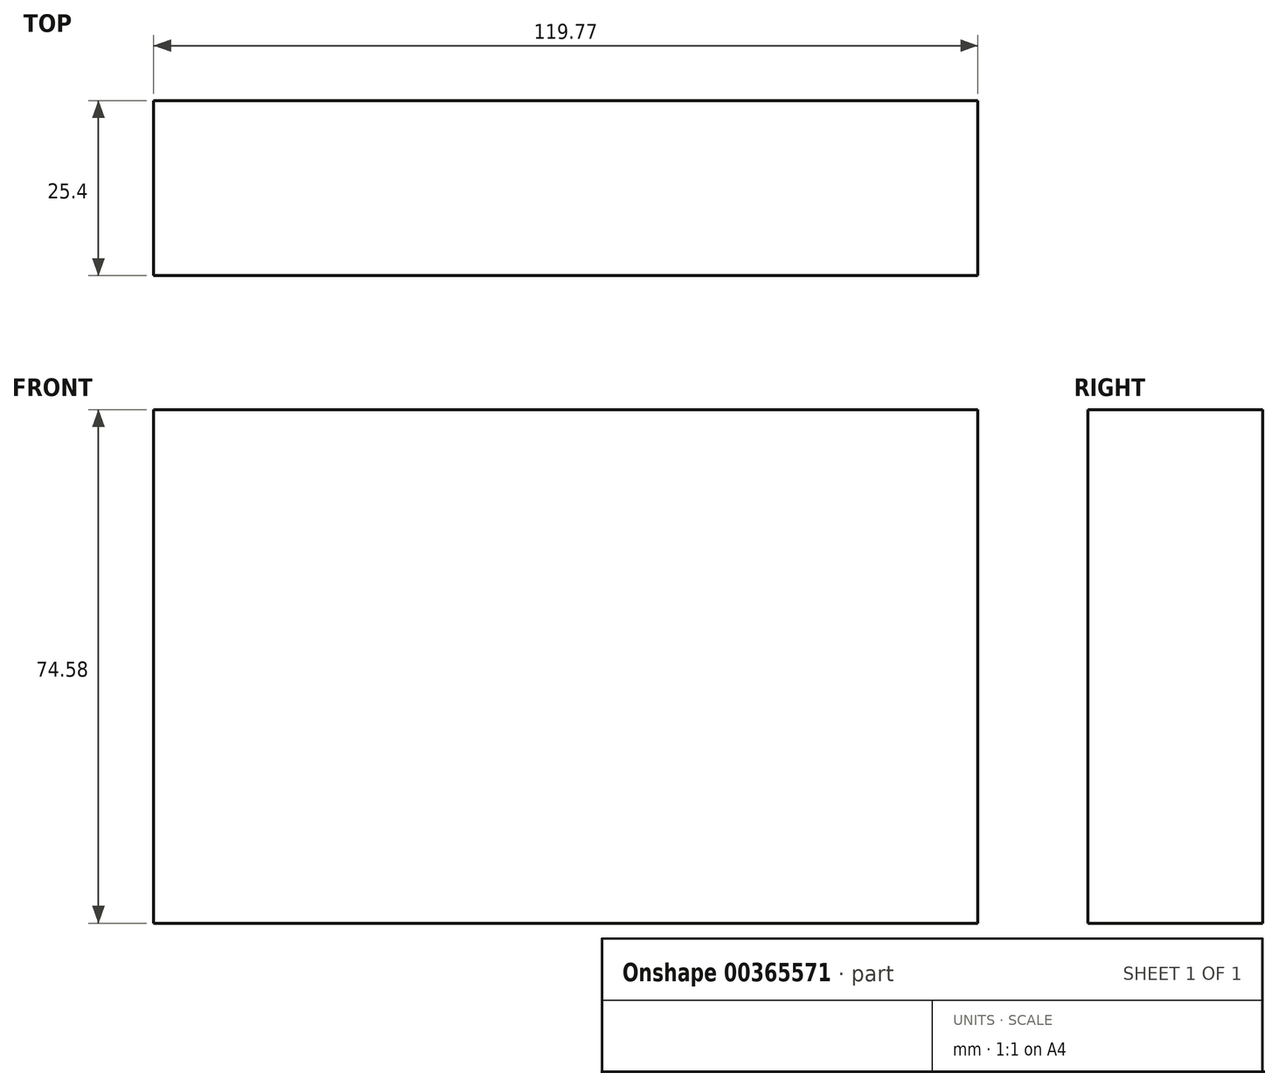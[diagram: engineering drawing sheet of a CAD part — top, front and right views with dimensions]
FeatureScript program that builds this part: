
annotation { "Feature Type Name" : "Feature", "Feature Type Description" : "" }
export const myFeature = defineFeature(function(context is Context, id is Id, definition is map)
    precondition{}
    {
        {
            var Q0;
            Q0=qCreatedBy(makeId("Front.planeOp"),FACE);
            var sketch = newSketch(context, id + "F0", { "sketchPlane" : qUnion([Q0])});
            skLineSegment(sketch, "E0.bottom", {"start": v(-57.04, 45.84) * mm, "end": v(62.73, 45.84) * mm});
            skLineSegment(sketch, "E0.top", {"start": v(-57.04, -28.74) * mm, "end": v(2.84, -28.74) * mm});
            skLineSegment(sketch, "E0.left", {"start": v(-57.04, 45.84) * mm, "end": v(-57.04, -28.74) * mm});
            skLineSegment(sketch, "E0.right", {"start": v(62.73, 45.84) * mm, "end": v(62.73, -28.74) * mm});
            skLineSegment(sketch, "E1", {"start": v(2.84, -28.74) * mm, "end": v(14.49, -28.74) * mm});
            skLineSegment(sketch, "E2", {"start": v(14.49, -28.74) * mm, "end": v(62.73, -28.74) * mm});
            skSolve(sketch);
        }
        {
            var Q0;
            Q0 = qSketchRegion(id + "F0", true);
            extrude(context, id + "F1", {"entities" : qUnion([Q0]), "depth" : 25.4 * mm});
        }
        {
            var Q0;
            Q0=qCreatedBy(makeId("Front.planeOp"),FACE);
            var sketch = newSketch(context, id + "F2", { "sketchPlane" : qUnion([Q0])});
            skLineSegment(sketch, "E3.bottom", {"start": v(0, 28.26) * mm, "end": v(54.96, 28.26) * mm});
            skLineSegment(sketch, "E3.top", {"start": v(0, 37.66) * mm, "end": v(54.96, 37.66) * mm});
            skLineSegment(sketch, "E3.left", {"start": v(0, 28.26) * mm, "end": v(0, 37.66) * mm});
            skLineSegment(sketch, "E3.right", {"start": v(54.96, 28.26) * mm, "end": v(54.96, 37.66) * mm});
            skSolve(sketch);
        }
        {
            var Q0;
            Q0 = qSketchRegion(id + "F2", true);
            extrude(context, id + "F3", {"entities" : qUnion([Q0]), "operationType" : NewBodyOperationType.ADD, "depth" : 25.4 * mm});
        }
    });
